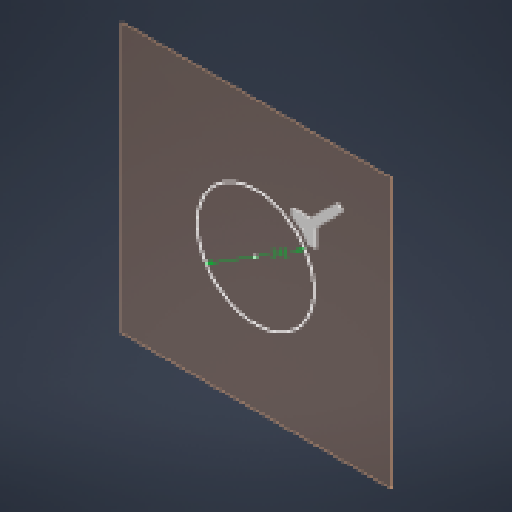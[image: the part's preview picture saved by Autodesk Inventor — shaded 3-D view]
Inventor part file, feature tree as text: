
AUTODESK INVENTOR PART (.ipt)
format: ipt  version: 2023.1 (Build 271208000, 208)  size: 142,848 bytes
history: native  units: mm
features: other x3, sketch x2, plane x1, extrude x1
ambient origin geometry x8: Origin, YZ Plane, XZ Plane, XY Plane, X Axis, Y Axis, Z Axis, Center Point
bodies: Body1 (feature_tree)
feature tree (7):
  plane  "Work Plane1"
  extrude  "Extrusion2"  Depth=10.0mm
  sketch  "Sketch4"  dims[d2=147.0mm d3=45.0deg d4=5.0mm d5=5.0mm d6=3.0mm d7=29.0mm d8=29.0mm d9=3.0mm d12=2.0mm d13=0.0mm d14=141.0mm]
  sketch  "Sketch1"  dims[d0=155.0mm d1=10.0mm]
  parser-record x1  (decoder bookkeeping rows leaked as tree rows — omitted from the tree; the rows remain in map.json)
  other  "Beau4tClock.iam"
  other  "Clock:1"
note: 1 file-system path scrubbed to <path> (originals preserved in map.json)
